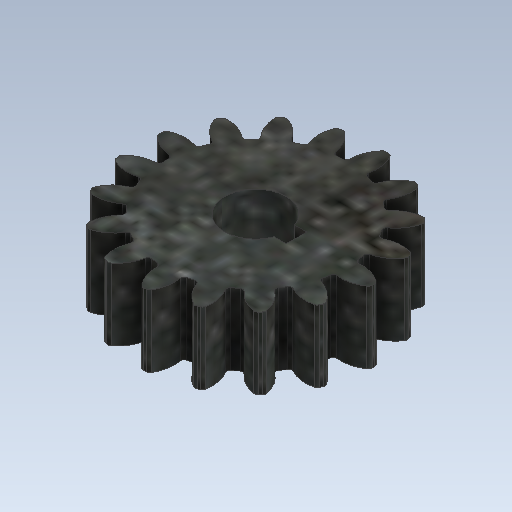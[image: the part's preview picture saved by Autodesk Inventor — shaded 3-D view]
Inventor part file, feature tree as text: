
AUTODESK INVENTOR PART (.ipt)
format: ipt  version: 2021 (Build 250183000, 183)  size: 411,136 bytes
history: native  units: mm
features: extrude x2, sketch x2, fillet x1, pattern_circular x1
ambient origin geometry x8: Origin, YZ Plane, XZ Plane, XY Plane, X Axis, Y Axis, Z Axis, Center Point
bodies: Solid1 (feature_tree)
feature tree (6):
  extrude  "Extrusion1"  Depth=7.0mm TaperAngle=360.0deg
  fillet  "Fillet2"  Radius=21.0mm
  pattern_circular  "Circular Pattern2"  [2 undecoded]
  extrude  "Extrusion6"  Depth=2.0mm
  sketch  "Sketch1"  dims[d4=7.0mm d5=0.0mm d18=170.0mm d19=360.0deg d23=21.0mm]
  sketch  "Sketch7"  dims[d25=1.544118mm d26=1.235294mm d27=3.490659mm d28=19.733545mm d29=3.490659mm d30=0.308824mm d31=0.617647mm d32=0.9702mm d33=0.4mm d87=6.0mm d88=2.0mm d89=2.0mm d90=2.0mm d91=0.0mm d92=0.0mm]
note: 2 required parameter values undecoded (feature->parameter linkage not recoverable at this tier; creation-order binding heuristic only, values carry confidence <= 0.55)
